# Revit family: Holocom-SLC Connector-2015
name_source: partatom
category: Security Devices
revit_build: Autodesk Revit 2015 (Build: 20140606_1530(x64)
units: mm (PartAtom-declared; Revit-internal decimal feet)

## types (8) — shared parameters
Default Elevation = 4' - 0"
Manufacturer = Holocom
Material = Holocom_WhiteTextured
Offset = 0' - 1"
URL = www.holocom.com

## per-type parameters (varying)
| type | Drop | Model | Product Page URL | Pull Box | Run End |
| 90 Deg Internal | No | SLC-CT-90i | http://holocom.com | No | No |
| 90 Deg External | No | SLC-CT-90e | http://holocom.com | No | No |
| Run End | No | SLC-CT-REC-LT_RT | http://holocom.com | No | Yes |
| Through-wall Run End | No | SLC-TWK-REC-LT_RT | http://holocom.com | No | No |
| Pull Box | No | SLC-WM-PB0-H1 | http://holocom.com | Yes | No |
| Through-wall Trim Plate | No | SLC-TWK-TP | http://holocom.com | No | No |
| Retrofit Interface Sleeve | No | SLC-RTF-INF-LT_RT | http://holocom.com | No | No |
| Drop | Yes | SLC-RTF-INF-LT_RT |  | No | No |

type visibility flags (boolean, named after types; folded from table):
- 90 Deg Internal: Yes: 90 Deg Internal
- 90 Deg External: Yes: 90 Deg External
- Run End: Yes: (none)
- Through-wall Run End: Yes: Through-wall Run End
- Pull Box: Yes: (none)
- Through-wall Trim Plate: Yes: Through-wall Trim Plate
- Retrofit Interface Sleeve: Yes: Retrofit Interface Sleeve
- Drop: Yes: (none)

## geometry (parser evidence)
native form markers: Sweep x24
no freeform markers — native parametric forms only
